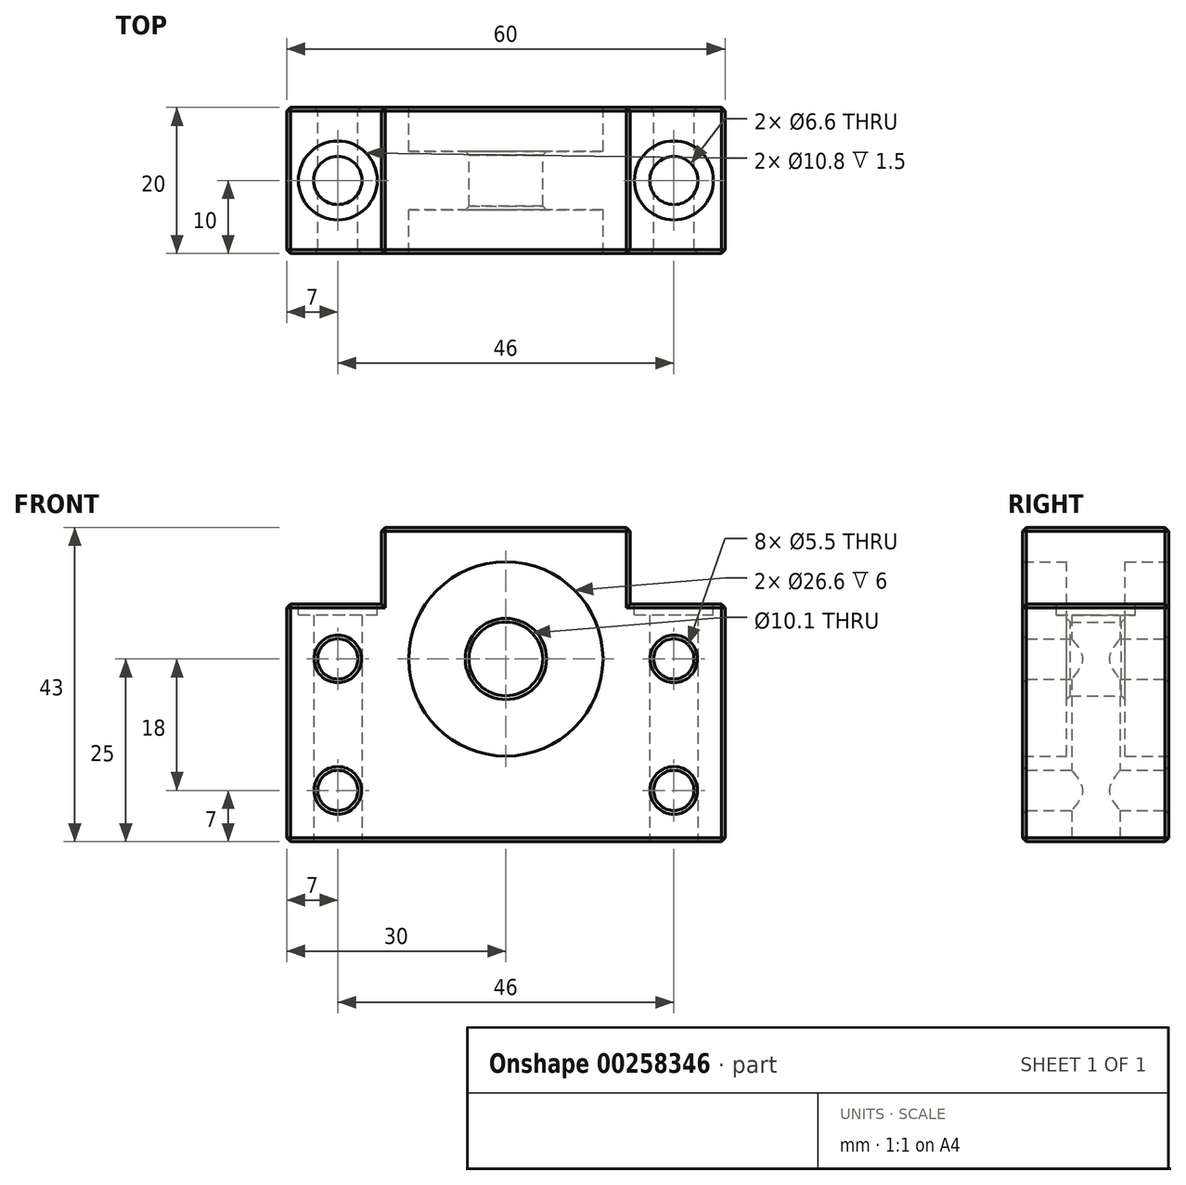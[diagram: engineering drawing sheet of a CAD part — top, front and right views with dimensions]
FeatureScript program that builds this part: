
annotation { "Feature Type Name" : "Feature", "Feature Type Description" : "" }
export const myFeature = defineFeature(function(context is Context, id is Id, definition is map)
    precondition{}
    {
        {
            var Q0;
            Q0=qCreatedBy(makeId("Front.planeOp"),FACE);
            var sketch = newSketch(context, id + "F0", { "sketchPlane" : qUnion([Q0])});
            skCircle(sketch, "E0", {"center": v(0, 0) * mm, "radius": 13.3 * mm});
            skSolve(sketch);
        }
        {
            var Q0;
            Q0=qCreatedBy(makeId("Front.planeOp"),FACE);
            var sketch = newSketch(context, id + "F1", { "sketchPlane" : qUnion([Q0])});
            skLineSegment(sketch, "E1", {"start": v(-30, 7.5) * mm, "end": v(-30, -25) * mm});
            skLineSegment(sketch, "E2", {"start": v(-30, -25) * mm, "end": v(30, -25) * mm});
            skLineSegment(sketch, "E3", {"start": v(30, -25) * mm, "end": v(30, 7.5) * mm});
            skLineSegment(sketch, "E4", {"start": v(30, 7.5) * mm, "end": v(17, 7.5) * mm});
            skLineSegment(sketch, "E5", {"start": v(17, 7.5) * mm, "end": v(17, 18) * mm});
            skLineSegment(sketch, "E6", {"start": v(17, 18) * mm, "end": v(-17, 18) * mm});
            skLineSegment(sketch, "E7", {"start": v(-17, 18) * mm, "end": v(-17, 7.5) * mm});
            skLineSegment(sketch, "E8", {"start": v(-17, 7.5) * mm, "end": v(-30, 7.5) * mm});
            skLineSegment(sketch, "E9", {"start": v(0, 18) * mm, "end": v(0, -25) * mm, "construction": true});
            skCircle(sketch, "E10", {"center": v(-23, 0) * mm, "radius": 2.75 * mm});
            skCircle(sketch, "E11", {"center": v(-23, -18) * mm, "radius": 2.75 * mm});
            skCircle(sketch, "E12", {"center": v(23, -18) * mm, "radius": 2.75 * mm});
            skCircle(sketch, "E13", {"center": v(23, 0) * mm, "radius": 2.75 * mm});
            skSolve(sketch);
        }
        {
            var Q0;
            Q0=qSketchRegion(id+"F1",true);
            extrude(context, id + "F2", {"entities" : qUnion([Q0]), "depth" : 20 * mm});
        }
        {
            var Q0;
            Q0=qSketchRegion(id+"F0",true);
            extrude(context, id + "F3", {"entities" : qUnion([Q0]), "operationType" : NewBodyOperationType.REMOVE, "endBound" : BoundingType.UP_TO_NEXT, "depth" : 25 * mm});
        }
        {
            var Q0;
            Q0=qCreatedBy(makeId("Front.planeOp"),FACE);
            cPlane(context, id + "F4", {"entities" : qUnion([Q0]), "cplaneType" : CPlaneType.OFFSET, "offset" : 6 * mm, "width" : 150 * mm, "height" : 150 * mm});
        }
        {
            var Q0;
            Q0=qCreatedBy(id+"F4.planeOp",FACE);
            var sketch = newSketch(context, id + "F5", { "sketchPlane" : qUnion([Q0])});
            skCircle(sketch, "E14", {"center": v(0, 0) * mm, "radius": 13.3 * mm});
            skCircle(sketch, "E15", {"center": v(0, 0) * mm, "radius": 5.05 * mm});
            skSolve(sketch);
        }
        {
            var Q0;
            Q0=qSketchRegion(id+"F5",true);
            extrude(context, id + "F6", {"entities" : qUnion([Q0]), "operationType" : NewBodyOperationType.ADD, "depth" : 8 * mm});
        }
        {
            var Q0;
            Q0=makeQuery(id+"F2.opExtrude","SWEPT_FACE",FACE,{"disambiguationData":[OSD([sQuery(id+"F1.wireOp",EDGE,"E2")])]});
            var sketch = newSketch(context, id + "F7", { "sketchPlane" : qUnion([Q0])});
            skLineSegment(sketch, "E16", {"start": v(0, 20) * mm, "end": v(0, 0) * mm, "construction": true});
            skLineSegment(sketch, "E17", {"start": v(-30, 10) * mm, "end": v(30, 10) * mm, "construction": true});
            skCircle(sketch, "E18", {"center": v(-23, 10) * mm, "radius": 3.3 * mm});
            skCircle(sketch, "E19", {"center": v(23, 10) * mm, "radius": 3.3 * mm});
            skSolve(sketch);
        }
        {
            var Q0;
            Q0=qSketchRegion(id+"F7",true);
            var Q1;
            Q1=makeQuery(id+"F2.opExtrude","SWEPT_FACE",FACE,{"disambiguationData":[OSD([sQuery(id+"F1.wireOp",EDGE,"E8")])]});
            extrude(context, id + "F8", {"entities" : qUnion([Q0]), "operationType" : NewBodyOperationType.REMOVE, "endBound" : BoundingType.UP_TO_SURFACE, "oppositeDirection" : true, "endBoundEntityFace" : qUnion([Q1]), "depth" : 25 * mm});
        }
        {
            var Q0;
            Q0=makeQuery(id+"F2.opExtrude","SWEPT_FACE",FACE,{"disambiguationData":[OSD([sQuery(id+"F1.wireOp",EDGE,"E8")])]});
            var sketch = newSketch(context, id + "F9", { "sketchPlane" : qUnion([Q0])});
            skCircle(sketch, "E20", {"center": v(-23, -10) * mm, "radius": 5.4 * mm});
            skCircle(sketch, "E21", {"center": v(23, -10) * mm, "radius": 5.4 * mm});
            skSolve(sketch);
        }
        {
            var Q0;
            Q0=qSketchRegion(id+"F9",true);
            extrude(context, id + "F10", {"entities" : qUnion([Q0]), "operationType" : NewBodyOperationType.REMOVE, "oppositeDirection" : true, "depth" : 1.5 * mm});
        }
        {
            var Q0;
            Q0=makeQuery(id+"F2.opExtrude","SWEPT_EDGE",EDGE,{"disambiguationData":[OSD([sQuery(id+"F1.wireOp",EDGE,"E6"),sQuery(id+"F1.wireOp",EDGE,"E7")])]});
            var Q1;
            Q1=makeQuery(id+"F2.opExtrude","CAP_EDGE",EDGE,{"disambiguationData":[OSD([sQuery(id+"F1.wireOp",EDGE,"E6")])],"isStart":false});
            var Q2;
            Q2=makeQuery(id+"F2.opExtrude","SWEPT_EDGE",EDGE,{"disambiguationData":[OSD([sQuery(id+"F1.wireOp",EDGE,"E5"),sQuery(id+"F1.wireOp",EDGE,"E6")])]});
            var Q3;
            Q3=makeQuery(id+"F2.opExtrude","CAP_EDGE",EDGE,{"disambiguationData":[OSD([sQuery(id+"F1.wireOp",EDGE,"E6")])],"isStart":true});
            var Q4;
            Q4=makeQuery(id+"F2.opExtrude","CAP_EDGE",EDGE,{"disambiguationData":[OSD([sQuery(id+"F1.wireOp",EDGE,"E8")])],"isStart":false});
            var Q5;
            Q5=makeQuery(id+"F2.opExtrude","SWEPT_EDGE",EDGE,{"disambiguationData":[OSD([sQuery(id+"F1.wireOp",EDGE,"E1"),sQuery(id+"F1.wireOp",EDGE,"E8")])]});
            var Q6;
            Q6=makeQuery(id+"F2.opExtrude","CAP_EDGE",EDGE,{"disambiguationData":[OSD([sQuery(id+"F1.wireOp",EDGE,"E8")])],"isStart":true});
            var Q7;
            Q7=makeQuery(id+"F2.opExtrude","CAP_EDGE",EDGE,{"disambiguationData":[OSD([sQuery(id+"F1.wireOp",EDGE,"E4")])],"isStart":false});
            var Q8;
            Q8=makeQuery(id+"F2.opExtrude","CAP_EDGE",EDGE,{"disambiguationData":[OSD([sQuery(id+"F1.wireOp",EDGE,"E5")])],"isStart":false});
            var Q9;
            Q9=makeQuery(id+"F2.opExtrude","CAP_EDGE",EDGE,{"disambiguationData":[OSD([sQuery(id+"F1.wireOp",EDGE,"E7")])],"isStart":false});
            var Q10;
            Q10=makeQuery(id+"F2.opExtrude","CAP_EDGE",EDGE,{"disambiguationData":[OSD([sQuery(id+"F1.wireOp",EDGE,"E1")])],"isStart":false});
            var Q11;
            Q11=makeQuery(id+"F2.opExtrude","CAP_EDGE",EDGE,{"disambiguationData":[OSD([sQuery(id+"F1.wireOp",EDGE,"E2")])],"isStart":false});
            var Q12;
            Q12=makeQuery(id+"F2.opExtrude","CAP_EDGE",EDGE,{"disambiguationData":[OSD([sQuery(id+"F1.wireOp",EDGE,"E11")])],"isStart":false});
            var Q13;
            Q13=makeQuery(id+"F2.opExtrude","CAP_EDGE",EDGE,{"disambiguationData":[OSD([sQuery(id+"F1.wireOp",EDGE,"E10")])],"isStart":false});
            var Q14;
            Q14=makeQuery(id+"F2.opExtrude","CAP_EDGE",EDGE,{"disambiguationData":[OSD([sQuery(id+"F1.wireOp",EDGE,"E13")])],"isStart":false});
            var Q15;
            Q15=makeQuery(id+"F2.opExtrude","CAP_EDGE",EDGE,{"disambiguationData":[OSD([sQuery(id+"F1.wireOp",EDGE,"E12")])],"isStart":false});
            var Q16;
            Q16=makeQuery(id+"F3.boolean.opBoolean","COPY",EDGE,{"derivedFrom":makeQuery(id+"F3.opExtrude","TWEAK_EDGE",EDGE,{"derivedFrom":[makeQuery(id+"F0.imprint","IMPRINT",EDGE,{"derivedFrom":sQuery(id+"F0.wireOp",EDGE,"E0")}),makeQuery(id+"F2.opExtrude","CAP_FACE",FACE,{"disambiguationData":[OSD([sQuery(id+"F1.wireOp",EDGE,"E1"),sQuery(id+"F1.wireOp",EDGE,"E2"),sQuery(id+"F1.wireOp",EDGE,"E3"),sQuery(id+"F1.wireOp",EDGE,"E4"),sQuery(id+"F1.wireOp",EDGE,"E5"),sQuery(id+"F1.wireOp",EDGE,"E6"),sQuery(id+"F1.wireOp",EDGE,"E7"),sQuery(id+"F1.wireOp",EDGE,"E8"),sQuery(id+"F1.wireOp",EDGE,"E10"),sQuery(id+"F1.wireOp",EDGE,"E11"),sQuery(id+"F1.wireOp",EDGE,"E12"),sQuery(id+"F1.wireOp",EDGE,"E13")])],"isStart":false})]})});
            var Q17;
            Q17=makeQuery(id+"F2.opExtrude","CAP_EDGE",EDGE,{"disambiguationData":[OSD([sQuery(id+"F1.wireOp",EDGE,"E3")])],"isStart":false});
            var Q18;
            Q18=makeQuery(id+"F2.opExtrude","SWEPT_EDGE",EDGE,{"disambiguationData":[OSD([sQuery(id+"F1.wireOp",EDGE,"E2"),sQuery(id+"F1.wireOp",EDGE,"E3")])]});
            var Q19;
            Q19=makeQuery(id+"F2.opExtrude","CAP_EDGE",EDGE,{"disambiguationData":[OSD([sQuery(id+"F1.wireOp",EDGE,"E3")])],"isStart":true});
            var Q20;
            Q20=makeQuery(id+"F2.opExtrude","SWEPT_EDGE",EDGE,{"disambiguationData":[OSD([sQuery(id+"F1.wireOp",EDGE,"E3"),sQuery(id+"F1.wireOp",EDGE,"E4")])]});
            var Q21;
            Q21=makeQuery(id+"F2.opExtrude","CAP_EDGE",EDGE,{"disambiguationData":[OSD([sQuery(id+"F1.wireOp",EDGE,"E4")])],"isStart":true});
            var Q22;
            Q22=makeQuery(id+"F2.opExtrude","CAP_EDGE",EDGE,{"disambiguationData":[OSD([sQuery(id+"F1.wireOp",EDGE,"E5")])],"isStart":true});
            var Q23;
            Q23=makeQuery(id+"F6.opExtrude","CAP_EDGE",EDGE,{"disambiguationData":[OSD([sQuery(id+"F5.wireOp",EDGE,"E15")])],"isStart":false});
            var Q24;
            Q24=makeQuery(id+"F2.opExtrude","CAP_EDGE",EDGE,{"disambiguationData":[OSD([sQuery(id+"F1.wireOp",EDGE,"E13")])],"isStart":true});
            var Q25;
            Q25=makeQuery(id+"F2.opExtrude","CAP_EDGE",EDGE,{"disambiguationData":[OSD([sQuery(id+"F1.wireOp",EDGE,"E12")])],"isStart":true});
            var Q26;
            Q26=makeQuery(id+"F2.opExtrude","CAP_EDGE",EDGE,{"disambiguationData":[OSD([sQuery(id+"F1.wireOp",EDGE,"E10")])],"isStart":true});
            var Q27;
            Q27=makeQuery(id+"F3.boolean.opBoolean","COPY",EDGE,{"derivedFrom":makeQuery(id+"F3.opExtrude","CAP_EDGE",EDGE,{"disambiguationData":[OSD([sQuery(id+"F0.wireOp",EDGE,"E0")])],"isStart":true})});
            var Q28;
            Q28=makeQuery(id+"F2.opExtrude","SWEPT_FACE",FACE,{"disambiguationData":[OSD([sQuery(id+"F1.wireOp",EDGE,"E1")])]});
            var Q29;
            Q29=makeQuery(id+"F2.opExtrude","CAP_EDGE",EDGE,{"disambiguationData":[OSD([sQuery(id+"F1.wireOp",EDGE,"E7")])],"isStart":true});
            var Q30;
            Q30=makeQuery(id+"F2.opExtrude","CAP_EDGE",EDGE,{"disambiguationData":[OSD([sQuery(id+"F1.wireOp",EDGE,"E11")])],"isStart":true});
            var Q31;
            Q31=makeQuery(id+"F2.opExtrude","CAP_EDGE",EDGE,{"disambiguationData":[OSD([sQuery(id+"F1.wireOp",EDGE,"E2")])],"isStart":true});
            var Q32;
            Q32=makeQuery(id+"F6.opExtrude","CAP_EDGE",EDGE,{"disambiguationData":[OSD([sQuery(id+"F5.wireOp",EDGE,"E15")])],"isStart":true});
            var Q33;
            Q33=makeQuery(id+"F8.boolean.opBoolean","COPY",EDGE,{"derivedFrom":makeQuery(id+"F8.opExtrude","CAP_EDGE",EDGE,{"disambiguationData":[OSD([sQuery(id+"F7.wireOp",EDGE,"E18")])],"isStart":true})});
            var Q34;
            Q34=makeQuery(id+"F8.boolean.opBoolean","COPY",EDGE,{"derivedFrom":makeQuery(id+"F8.opExtrude","CAP_EDGE",EDGE,{"disambiguationData":[OSD([sQuery(id+"F7.wireOp",EDGE,"E19")])],"isStart":true})});
            chamfer(context, id + "F11", {"entities" : qUnion([Q0, Q1, Q2, Q3, Q4, Q5, Q6, Q7, Q8, Q9, Q10, Q11, Q12, Q13, Q14, Q15, Q16, Q17, Q18, Q19, Q20, Q21, Q22, Q23, Q24, Q25, Q26, Q27, Q28, Q29, Q30, Q31, Q32, Q33, Q34]), "width" : 0.5 * mm, "tangentPropagation" : true});
        }
    });
